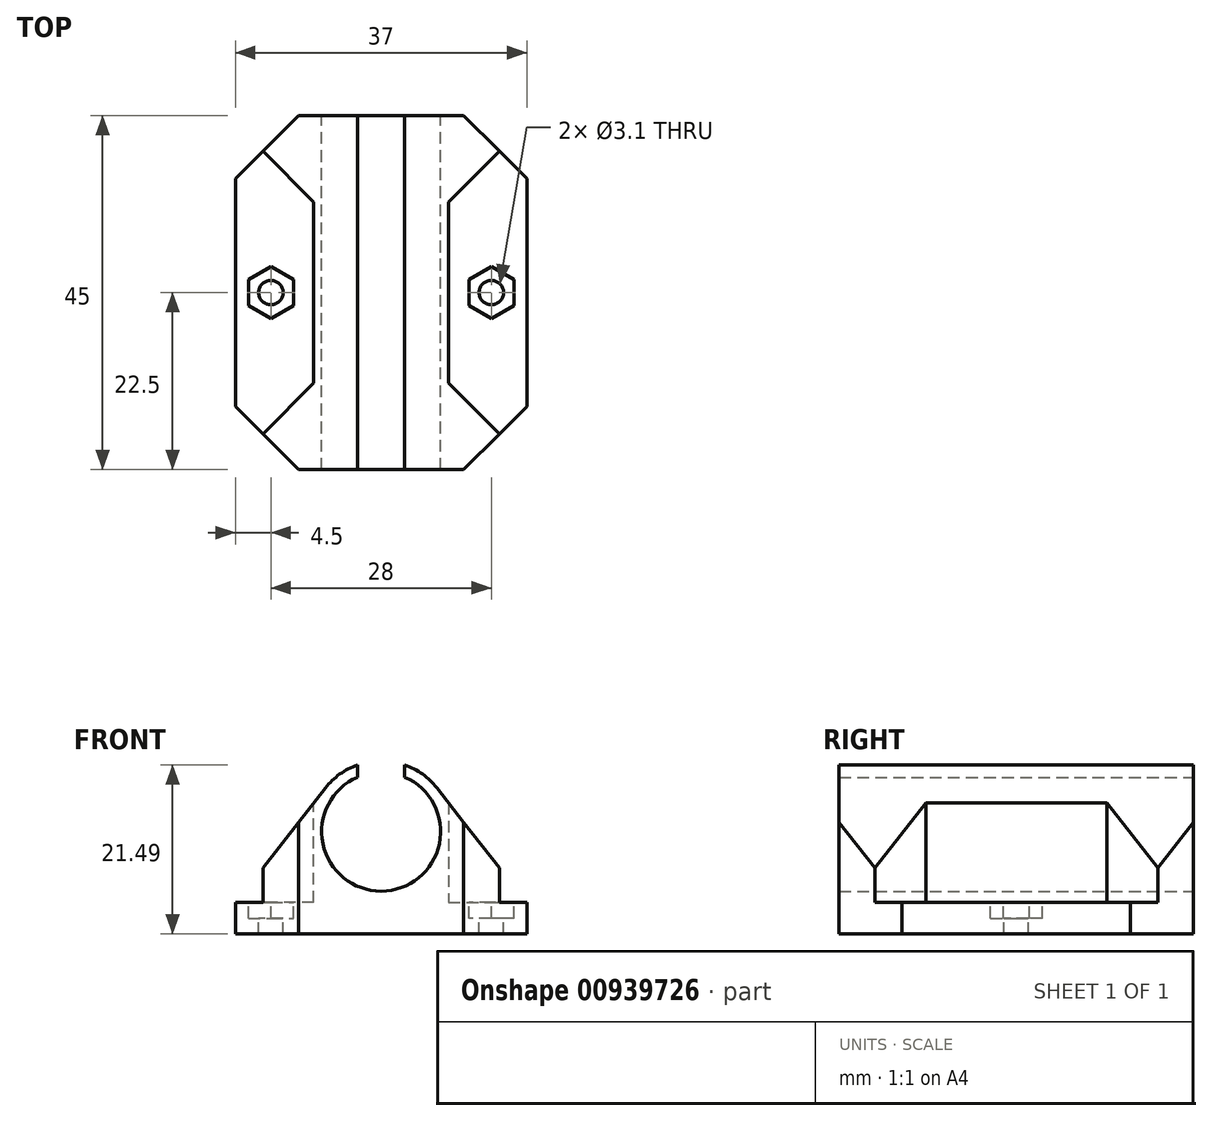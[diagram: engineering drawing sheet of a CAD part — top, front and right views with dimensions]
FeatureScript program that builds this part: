
annotation { "Feature Type Name" : "Feature", "Feature Type Description" : "" }
export const myFeature = defineFeature(function(context is Context, id is Id, definition is map)
    precondition{}
    {
        {
            var Q0;
            Q0=qCreatedBy(makeId("Front.planeOp"),FACE);
            var sketch = newSketch(context, id + "F0", { "sketchPlane" : qUnion([Q0])});
            skCircle(sketch, "E0", {"center": v(0, 13) * mm, "radius": 7.55 * mm});
            skCircle(sketch, "E1", {"center": v(0, 13) * mm, "radius": 9 * mm});
            skLineSegment(sketch, "E2", {"start": v(-7.08, 18.56) * mm, "end": v(-18.5, 4) * mm});
            skLineSegment(sketch, "E3", {"start": v(-18.5, 4) * mm, "end": v(-18.5, 0) * mm});
            skLineSegment(sketch, "E4", {"start": v(-18.5, 0) * mm, "end": v(18.5, 0) * mm});
            skLineSegment(sketch, "E5", {"start": v(18.5, 0) * mm, "end": v(18.5, 4) * mm});
            skLineSegment(sketch, "E6", {"start": v(18.5, 4) * mm, "end": v(7.08, 18.56) * mm});
            skLineSegment(sketch, "E7", {"start": v(-3, 21.49) * mm, "end": v(-3, 19.93) * mm});
            skLineSegment(sketch, "E8", {"start": v(3, 21.49) * mm, "end": v(3, 19.93) * mm});
            skSolve(sketch);
        }
        {
            var Q0;
            {var subQ0=sQuery(id+"F0.wireOp",EDGE,"E2");Q0=makeQuery(id+"F0.imprint","IMPRINT",FACE,{"disambiguationData":[TD([[makeQuery(id+"F0.imprint","IMPRINT",EDGE,{"derivedFrom":subQ0}),1.0]])]});}
            var Q1;
            {var subQ3=sQuery(id+"F0.wireOp",EDGE,"E7");Q1=makeQuery(id+"F0.imprint","IMPRINT",FACE,{"disambiguationData":[TD([[makeQuery(id+"F0.imprint","IMPRINT",EDGE,{"derivedFrom":subQ3}),-1.0]])]});}
            extrude(context, id + "F1", {"entities" : qUnion([Q0, Q1]), "depth" : 45 * mm, "offsetDistance" : 25 * mm, "symmetric" : true});
        }
        {
            var Q0;
            Q0=qCreatedBy(makeId("Top.planeOp"),FACE);
            cPlane(context, id + "F2", {"entities" : qUnion([Q0]), "cplaneType" : CPlaneType.OFFSET, "offset" : 4 * mm, "width" : 150 * mm, "height" : 150 * mm});
        }
        {
            var Q0;
            Q0=qCreatedBy(id+"F2.planeOp",FACE);
            var sketch = newSketch(context, id + "F3", { "sketchPlane" : qUnion([Q0])});
            skLineSegment(sketch, "E9.0", {"start": v(7.55, -22.5) * mm, "end": v(-7.55, -22.5) * mm, "construction": true});
            skLineSegment(sketch, "E10.0", {"start": v(-18.5, -22.5) * mm, "end": v(-18.5, 22.5) * mm, "construction": true});
            skLineSegment(sketch, "E11.0", {"start": v(18.5, -22.5) * mm, "end": v(18.5, 22.5) * mm, "construction": true});
            skLineSegment(sketch, "E12.bottom", {"start": v(-18.5, 19.5) * mm, "end": v(-7.55, 19.5) * mm});
            skLineSegment(sketch, "E12.top", {"start": v(-18.5, -19.5) * mm, "end": v(-7.55, -19.5) * mm});
            skLineSegment(sketch, "E12.left", {"start": v(-18.5, 19.5) * mm, "end": v(-18.5, -19.5) * mm});
            skLineSegment(sketch, "E12.right", {"start": v(-7.55, 19.5) * mm, "end": v(-7.55, -19.5) * mm, "construction": true});
            skLineSegment(sketch, "E13.bottom", {"start": v(7.55, -19.5) * mm, "end": v(18.5, -19.5) * mm});
            skLineSegment(sketch, "E13.top", {"start": v(7.55, 19.5) * mm, "end": v(18.5, 19.5) * mm});
            skLineSegment(sketch, "E13.left", {"start": v(7.55, -19.5) * mm, "end": v(7.55, 19.5) * mm, "construction": true});
            skLineSegment(sketch, "E13.right", {"start": v(18.5, -19.5) * mm, "end": v(18.5, 19.5) * mm});
            skLineSegment(sketch, "E14", {"start": v(-8.55, -19.5) * mm, "end": v(-8.55, 19.5) * mm});
            skLineSegment(sketch, "E15", {"start": v(8.55, -19.5) * mm, "end": v(8.55, 19.5) * mm});
            skSolve(sketch);
        }
        {
            var Q0;
            Q0 = qSketchRegion(id + "F3", true);
            extrude(context, id + "F4", {"entities" : qUnion([Q0]), "operationType" : NewBodyOperationType.REMOVE, "endBound" : BoundingType.UP_TO_NEXT, "depth" : 25 * mm, "offsetDistance" : 25 * mm});
        }
        {
            var Q0;
            Q0=makeQuery(id+"F4.boolean.opBoolean","COPY",FACE,{"derivedFrom":makeQuery(id+"F4.opExtrude","CAP_FACE",FACE,{"disambiguationData":[OSD([sQuery(id+"F3.wireOp",EDGE,"E12.bottom"),sQuery(id+"F3.wireOp",EDGE,"E12.top"),sQuery(id+"F3.wireOp",EDGE,"E12.left"),sQuery(id+"F3.wireOp",EDGE,"E14")])],"isStart":true})});
            var sketch = newSketch(context, id + "F5", { "sketchPlane" : qUnion([Q0])});
            skCircle(sketch, "E16", {"center": v(-14, 0) * mm, "radius": 1.55 * mm});
            skCircle(sketch, "E17", {"center": v(14, 0) * mm, "radius": 1.55 * mm});
            skCircle(sketch, "E18.cCircle", {"center": v(14, 0) * mm, "radius": 2.85 * mm, "construction": true});
            skLineSegment(sketch, "E18.0", {"start": v(11.15, -1.65) * mm, "end": v(11.15, 1.65) * mm});
            skLineSegment(sketch, "E18.1", {"start": v(11.15, 1.65) * mm, "end": v(14, 3.3) * mm});
            skLineSegment(sketch, "E18.2", {"start": v(14, 3.3) * mm, "end": v(16.85, 1.65) * mm});
            skLineSegment(sketch, "E18.3", {"start": v(16.85, 1.65) * mm, "end": v(16.85, -1.65) * mm});
            skLineSegment(sketch, "E18.4", {"start": v(16.85, -1.65) * mm, "end": v(14, -3.3) * mm});
            skLineSegment(sketch, "E18.5", {"start": v(14, -3.3) * mm, "end": v(11.15, -1.65) * mm});
            skPoint(sketch, "E18.0.midPoint", {"position": v(11.15, 0) * mm});
            skCircle(sketch, "E19.cCircle", {"center": v(-14, 0) * mm, "radius": 2.85 * mm, "construction": true});
            skLineSegment(sketch, "E19.0", {"start": v(-11.15, 1.65) * mm, "end": v(-11.15, -1.65) * mm});
            skLineSegment(sketch, "E19.1", {"start": v(-11.15, -1.65) * mm, "end": v(-14, -3.3) * mm});
            skLineSegment(sketch, "E19.2", {"start": v(-14, -3.3) * mm, "end": v(-16.85, -1.65) * mm});
            skLineSegment(sketch, "E19.3", {"start": v(-16.85, -1.65) * mm, "end": v(-16.85, 1.65) * mm});
            skLineSegment(sketch, "E19.4", {"start": v(-16.85, 1.65) * mm, "end": v(-14, 3.3) * mm});
            skLineSegment(sketch, "E19.5", {"start": v(-14, 3.3) * mm, "end": v(-11.15, 1.65) * mm});
            skPoint(sketch, "E19.0.midPoint", {"position": v(-11.15, 0) * mm});
            skSolve(sketch);
        }
        {
            var Q0;
            Q0=makeQuery(id+"F5.imprint","IMPRINT",FACE,{"disambiguationData":[TD([[makeQuery(id+"F5.imprint","IMPRINT",EDGE,{"derivedFrom":sQuery(id+"F5.wireOp",EDGE,"E17")}),1.0]])]});
            var Q1;
            Q1=makeQuery(id+"F5.imprint","IMPRINT",FACE,{"disambiguationData":[TD([[makeQuery(id+"F5.imprint","IMPRINT",EDGE,{"derivedFrom":sQuery(id+"F5.wireOp",EDGE,"E16")}),1.0]])]});
            extrude(context, id + "F6", {"entities" : qUnion([Q0, Q1]), "operationType" : NewBodyOperationType.REMOVE, "endBound" : BoundingType.UP_TO_NEXT, "oppositeDirection" : true, "depth" : 25 * mm, "offsetDistance" : 25 * mm});
        }
        {
            var Q0;
            Q0=makeQuery(id+"F5.imprint","IMPRINT",FACE,{"disambiguationData":[TD([[makeQuery(id+"F5.imprint","IMPRINT",EDGE,{"derivedFrom":sQuery(id+"F5.wireOp",EDGE,"E17")}),-1.0]])]});
            var Q1;
            Q1=makeQuery(id+"F5.imprint","IMPRINT",FACE,{"disambiguationData":[TD([[makeQuery(id+"F5.imprint","IMPRINT",EDGE,{"derivedFrom":sQuery(id+"F5.wireOp",EDGE,"E16")}),-1.0]])]});
            extrude(context, id + "F7", {"entities" : qUnion([Q0, Q1]), "operationType" : NewBodyOperationType.REMOVE, "oppositeDirection" : true, "depth" : 2 * mm, "offsetDistance" : 25 * mm});
        }
        {
            var Q0;
            Q0=makeQuery(id+"F4.boolean.opBoolean","COPY",EDGE,{"derivedFrom":makeQuery(id+"F4.opExtrude","SWEPT_EDGE",EDGE,{"disambiguationData":[OSD([sQuery(id+"F3.wireOp",EDGE,"E12.bottom"),sQuery(id+"F3.wireOp",EDGE,"E14")])]})});
            var Q1;
            Q1=makeQuery(id+"F4.boolean.opBoolean","COPY",EDGE,{"derivedFrom":makeQuery(id+"F4.opExtrude","SWEPT_EDGE",EDGE,{"disambiguationData":[OSD([sQuery(id+"F3.wireOp",EDGE,"E12.top"),sQuery(id+"F3.wireOp",EDGE,"E14")])]})});
            var Q2;
            Q2=makeQuery(id+"F4.boolean.opBoolean","COPY",EDGE,{"derivedFrom":makeQuery(id+"F4.opExtrude","SWEPT_EDGE",EDGE,{"disambiguationData":[OSD([sQuery(id+"F3.wireOp",EDGE,"E13.top"),sQuery(id+"F3.wireOp",EDGE,"E15")])]})});
            var Q3;
            Q3=makeQuery(id+"F4.boolean.opBoolean","COPY",EDGE,{"derivedFrom":makeQuery(id+"F4.opExtrude","SWEPT_EDGE",EDGE,{"disambiguationData":[OSD([sQuery(id+"F3.wireOp",EDGE,"E13.bottom"),sQuery(id+"F3.wireOp",EDGE,"E15")])]})});
            chamfer(context, id + "F8", {"entities" : qUnion([Q0, Q1, Q2, Q3]), "chamferType" : ChamferType.OFFSET_ANGLE, "width" : 8 * mm, "oppositeDirection" : false, "angle" : 45 * degree, "tangentPropagation" : true});
        }
        {
            var Q0;
            Q0=makeQuery(id+"F1.opExtrude","CAP_EDGE",EDGE,{"disambiguationData":[OSD([sQuery(id+"F0.wireOp",EDGE,"E3")])],"isStart":true});
            var Q1;
            Q1=makeQuery(id+"F1.opExtrude","CAP_EDGE",EDGE,{"disambiguationData":[OSD([sQuery(id+"F0.wireOp",EDGE,"E3")])],"isStart":false});
            var Q2;
            Q2=makeQuery(id+"F1.opExtrude","CAP_EDGE",EDGE,{"disambiguationData":[OSD([sQuery(id+"F0.wireOp",EDGE,"E5")])],"isStart":true});
            var Q3;
            Q3=makeQuery(id+"F1.opExtrude","CAP_EDGE",EDGE,{"disambiguationData":[OSD([sQuery(id+"F0.wireOp",EDGE,"E5")])],"isStart":false});
            chamfer(context, id + "F9", {"entities" : qUnion([Q0, Q1, Q2, Q3]), "width" : 8 * mm, "tangentPropagation" : true});
        }
    });
